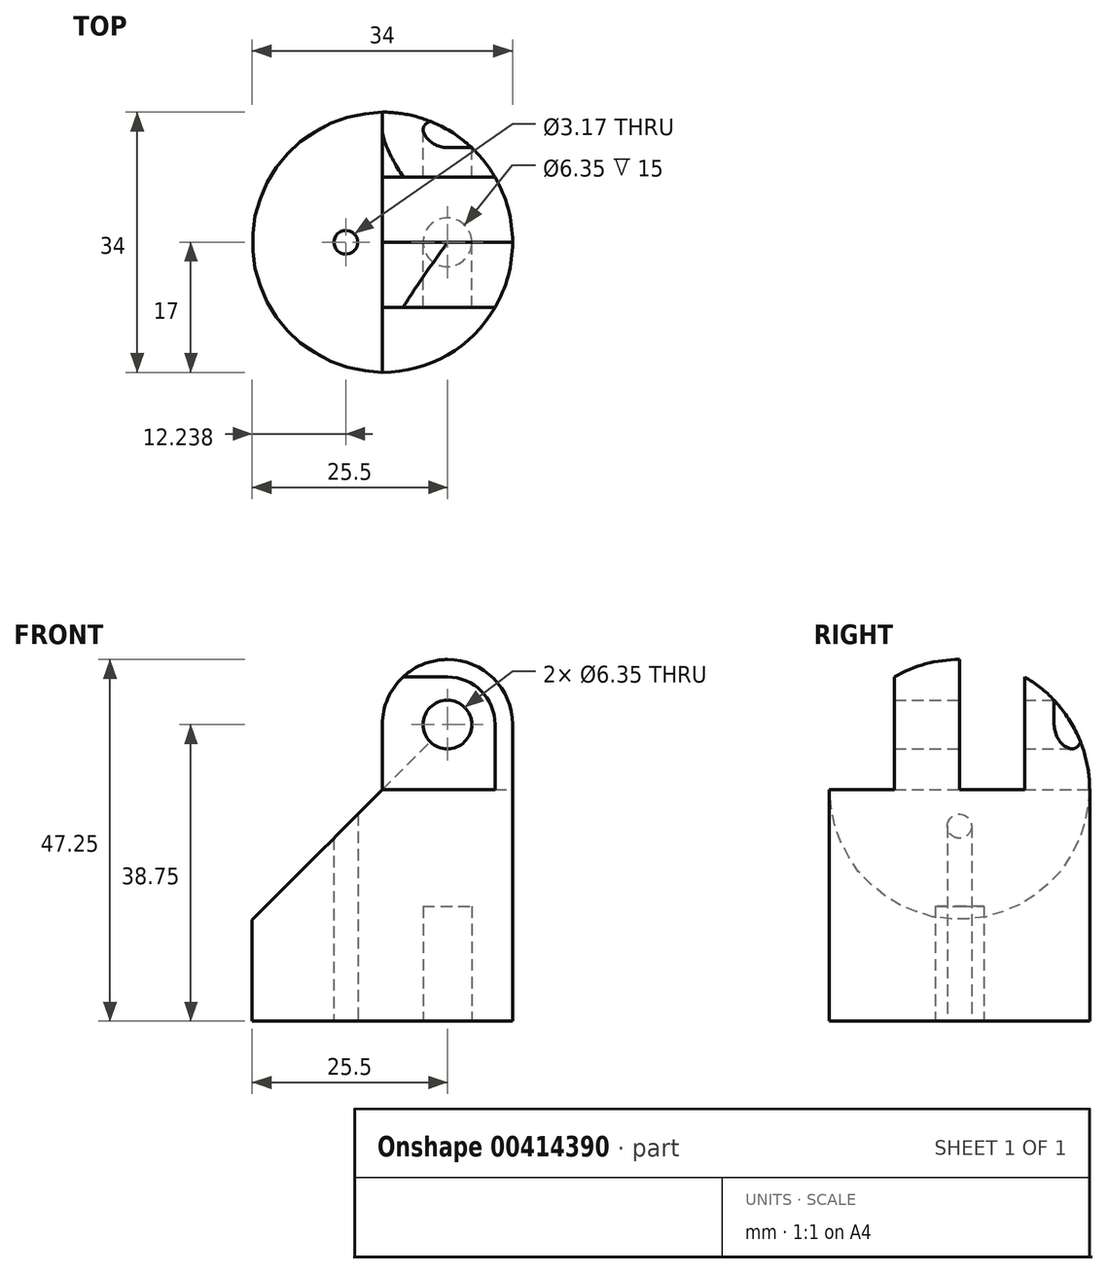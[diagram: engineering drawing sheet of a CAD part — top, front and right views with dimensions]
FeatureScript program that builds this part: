
annotation { "Feature Type Name" : "Feature", "Feature Type Description" : "" }
export const myFeature = defineFeature(function(context is Context, id is Id, definition is map)
    precondition{}
    {
        {
            var Q0;
            Q0=qCreatedBy(makeId("Top.planeOp"),FACE);
            var sketch = newSketch(context, id + "F0", { "sketchPlane" : qUnion([Q0])});
            skCircle(sketch, "E0", {"center": v(0, 0) * mm, "radius": 17 * mm});
            skSolve(sketch);
        }
        {
            var Q0;
            Q0 = qSketchRegion(id + "F0", true);
            extrude(context, id + "F1", {"entities" : qUnion([Q0]), "offsetDistance" : 25 * mm, "depth" : 13.25 * mm});
        }
        {
            var Q0;
            Q0=qCreatedBy(makeId("Front.planeOp"),FACE);
            var sketch = newSketch(context, id + "F2", { "sketchPlane" : qUnion([Q0])});
            skLineSegment(sketch, "E1", {"start": v(17, 38.75) * mm, "end": v(17, 13.25) * mm});
            skLineSegment(sketch, "E2", {"start": v(17, 13.25) * mm, "end": v(-17, 13.25) * mm});
            skLineSegment(sketch, "E3", {"start": v(-17, 13.25) * mm, "end": v(0, 30.25) * mm});
            skLineSegment(sketch, "E4", {"start": v(0, 30.25) * mm, "end": v(0, 38.75) * mm});
            skArc(sketch, "E5", {"start": v(0, 38.75) * mm, "mid": v(8.5, 47.25) * mm, "end": v(17, 38.75) * mm});
            skPoint(sketch, "E6", {"position": v(0, 13.25) * mm});
            skCircle(sketch, "E7", {"center": v(8.5, 38.75) * mm, "radius": 3.18 * mm});
            skSolve(sketch);
        }
        {
            var Q0;
            Q0 = qSketchRegion(id + "F2", true);
            var Q1;
            Q1=makeQuery(id+"F1.opExtrude","SWEPT_FACE",FACE,{"disambiguationData":[OSD([sQuery(id+"F0.wireOp",EDGE,"E0")])]});
            extrude(context, id + "F3", {"entities" : qUnion([Q0]), "operationType" : NewBodyOperationType.ADD, "endBound" : BoundingType.UP_TO_SURFACE, "endBoundEntityFace" : qUnion([Q1]), "depth" : 25 * mm});
        }
        {
            var Q0;
            Q0 = qSketchRegion(id + "F2", true);
            var Q1;
            {var subQ0=sQuery(id+"F0.wireOp",EDGE,"E0");Q1=makeQuery(id+"F3.boolean.opBoolean","MERGE",FACE,{"derivedFrom":[makeQuery(id+"F1.opExtrude","SWEPT_FACE",FACE,{"disambiguationData":[OSD([subQ0])]}),makeQuery(id+"F3.opExtrude","CAP_FACE",FACE,{"disambiguationData":[OSD([subQ0])],"isStart":false})]});}
            extrude(context, id + "F4", {"entities" : qUnion([Q0]), "operationType" : NewBodyOperationType.ADD, "endBound" : BoundingType.UP_TO_SURFACE, "oppositeDirection" : true, "endBoundEntityFace" : qUnion([Q1]), "depth" : 25 * mm});
        }
        {
            var Q0;
            Q0=qCreatedBy(makeId("Top.planeOp"),FACE);
            cPlane(context, id + "F5", {"entities" : qUnion([Q0]), "cplaneType" : CPlaneType.OFFSET, "offset" : 54 * mm, "width" : 150 * mm, "height" : 150 * mm});
        }
        {
            var Q0;
            Q0=qCreatedBy(id+"F5.planeOp",FACE);
            var sketch = newSketch(context, id + "F6", { "sketchPlane" : qUnion([Q0])});
            skLineSegment(sketch, "E8.bottom", {"start": v(0, 0) * mm, "end": v(17, 0) * mm});
            skLineSegment(sketch, "E8.top", {"start": v(0, 8.5) * mm, "end": v(17, 8.5) * mm});
            skLineSegment(sketch, "E8.left", {"start": v(0, 0) * mm, "end": v(0, 8.5) * mm});
            skLineSegment(sketch, "E8.right", {"start": v(17, 0) * mm, "end": v(17, 8.5) * mm});
            skLineSegment(sketch, "E9.bottom", {"start": v(0, -17) * mm, "end": v(17, -17) * mm});
            skLineSegment(sketch, "E9.top", {"start": v(0, -8.5) * mm, "end": v(17, -8.5) * mm});
            skLineSegment(sketch, "E9.left", {"start": v(0, -17) * mm, "end": v(0, -8.5) * mm});
            skLineSegment(sketch, "E9.right", {"start": v(17, -17) * mm, "end": v(17, -8.5) * mm});
            skLineSegment(sketch, "E10", {"start": v(0, 0) * mm, "end": v(0, 17) * mm});
            skSolve(sketch);
        }
        {
            var Q0;
            Q0 = qSketchRegion(id + "F6", true);
            var Q1;
            Q1=makeQuery(id+"F3.opExtrude","CAP_VERTEX",VERTEX,{"disambiguationData":[OSD([sQuery(id+"F0.wireOp",EDGE,"E0"),sQuery(id+"F2.wireOp",EDGE,"E3"),sQuery(id+"F2.wireOp",EDGE,"E4")])],"isStart":false});
            extrude(context, id + "F7", {"entities" : qUnion([Q0]), "operationType" : NewBodyOperationType.REMOVE, "endBound" : BoundingType.UP_TO_VERTEX, "oppositeDirection" : true, "endBoundEntityVertex" : qUnion([Q1]), "depth" : 10 * mm});
        }
        {
            var Q0;
            Q0=qCreatedBy(makeId("Top.planeOp"),FACE);
            var sketch = newSketch(context, id + "F8", { "sketchPlane" : qUnion([Q0])});
            skCircle(sketch, "E11", {"center": v(-4.76, 0) * mm, "radius": 1.59 * mm});
            skLineSegment(sketch, "E12", {"start": v(0, 0) * mm, "end": v(-17, 0) * mm});
            skSolve(sketch);
        }
        {
            var Q0;
            Q0 = qSketchRegion(id + "F8", true);
            extrude(context, id + "F9", {"entities" : qUnion([Q0]), "operationType" : NewBodyOperationType.REMOVE, "endBound" : BoundingType.THROUGH_ALL, "depth" : 25 * mm});
        }
        {
            var Q0;
            Q0=makeQuery(id+"F1.opExtrude","CAP_FACE",FACE,{"disambiguationData":[OSD([sQuery(id+"F0.wireOp",EDGE,"E0")])],"isStart":true});
            var sketch = newSketch(context, id + "F10", { "sketchPlane" : qUnion([Q0])});
            skCircle(sketch, "E13", {"center": v(8.5, 0) * mm, "radius": 3.18 * mm});
            skLineSegment(sketch, "E14", {"start": v(0, 0) * mm, "end": v(17, 0) * mm});
            skSolve(sketch);
        }
        {
            var Q0;
            Q0 = qSketchRegion(id + "F10", true);
            extrude(context, id + "F11", {"entities" : qUnion([Q0]), "operationType" : NewBodyOperationType.REMOVE, "oppositeDirection" : true, "depth" : 15 * mm});
        }
        {
            var Q0;
            Q0=qCreatedBy(makeId("Right.planeOp"),FACE);
            cPlane(context, id + "F12", {"entities" : qUnion([Q0]), "cplaneType" : CPlaneType.OFFSET, "offset" : 8.5 * mm, "width" : 150 * mm, "height" : 150 * mm});
        }
        {
            var Q0;
            Q0=qCreatedBy(id+"F12.planeOp",FACE);
            var sketch = newSketch(context, id + "F13", { "sketchPlane" : qUnion([Q0])});
            skLineSegment(sketch, "E15.bottom", {"start": v(17, 30.25) * mm, "end": v(-17, 30.25) * mm});
            skLineSegment(sketch, "E15.top", {"start": v(17, 47.25) * mm, "end": v(-17, 47.25) * mm});
            skLineSegment(sketch, "E15.left", {"start": v(17, 30.25) * mm, "end": v(17, 47.25) * mm});
            skLineSegment(sketch, "E15.right", {"start": v(-17, 30.25) * mm, "end": v(-17, 47.25) * mm});
            skArc(sketch, "E16", {"start": v(17, 30.25) * mm, "mid": v(0, 47.25) * mm, "end": v(-17, 30.25) * mm});
            skLineSegment(sketch, "E17", {"start": v(17, 38.75) * mm, "end": v(-17, 38.75) * mm});
            skSolve(sketch);
        }
        {
            var Q0;
            {var subQ0=sQuery(id+"F13.wireOp",EDGE,"E15.left");Q0=makeQuery(id+"F13.imprint","IMPRINT",FACE,{"disambiguationData":[TD([[makeQuery(id+"F13.imprint","IMPRINT",EDGE,{"derivedFrom":subQ0}),1.0]])]});}
            var Q1;
            {var subQ0=sQuery(id+"F13.wireOp",EDGE,"E15.right");Q1=makeQuery(id+"F13.imprint","IMPRINT",FACE,{"disambiguationData":[TD([[makeQuery(id+"F13.imprint","IMPRINT",EDGE,{"derivedFrom":subQ0}),-1.0]])]});}
            var Q2;
            {var subQ0=sQuery(id+"F13.wireOp",EDGE,"E15.right");var subQ1=sQuery(id+"F13.wireOp",EDGE,"E15.top");var subQ2=makeQuery(id+"F13.imprint","INTERSECT",VERTEX,{"derivedFrom":[subQ1,subQ0]});Q2=makeQuery(id+"F13.imprint","IMPRINT",FACE,{"disambiguationData":[TD([[makeQuery(id+"F13.imprint","IMPRINT",EDGE,{"disambiguationData":[TD([[subQ2,1.0]])],"derivedFrom":subQ1}),1.0]])]});}
            var Q3;
            {var subQ0=sQuery(id+"F13.wireOp",EDGE,"E15.left");var subQ1=sQuery(id+"F13.wireOp",EDGE,"E15.top");var subQ2=makeQuery(id+"F13.imprint","INTERSECT",VERTEX,{"derivedFrom":[subQ1,subQ0]});Q3=makeQuery(id+"F13.imprint","IMPRINT",FACE,{"disambiguationData":[TD([[makeQuery(id+"F13.imprint","IMPRINT",EDGE,{"disambiguationData":[TD([[subQ2,-1.0]])],"derivedFrom":subQ1}),1.0]])]});}
            extrude(context, id + "F14", {"entities" : qUnion([Q0, Q1, Q2, Q3]), "operationType" : NewBodyOperationType.REMOVE, "oppositeDirection" : true, "depth" : 34 * mm});
        }
        {
            var Q0;
            {var subQ0=sQuery(id+"F13.wireOp",EDGE,"E15.left");var subQ1=sQuery(id+"F13.wireOp",EDGE,"E15.top");var subQ2=makeQuery(id+"F13.imprint","INTERSECT",VERTEX,{"derivedFrom":[subQ1,subQ0]});Q0=makeQuery(id+"F13.imprint","IMPRINT",FACE,{"disambiguationData":[TD([[makeQuery(id+"F13.imprint","IMPRINT",EDGE,{"disambiguationData":[TD([[subQ2,-1.0]])],"derivedFrom":subQ1}),1.0]])]});}
            var Q1;
            {var subQ0=sQuery(id+"F13.wireOp",EDGE,"E15.right");var subQ1=sQuery(id+"F13.wireOp",EDGE,"E15.top");var subQ2=makeQuery(id+"F13.imprint","INTERSECT",VERTEX,{"derivedFrom":[subQ1,subQ0]});Q1=makeQuery(id+"F13.imprint","IMPRINT",FACE,{"disambiguationData":[TD([[makeQuery(id+"F13.imprint","IMPRINT",EDGE,{"disambiguationData":[TD([[subQ2,1.0]])],"derivedFrom":subQ1}),1.0]])]});}
            var Q2;
            Q2=sQuery(id+"F13.wireOp",EDGE,"E17");
            revolve(context, id + "F15", {"operationType" : NewBodyOperationType.REMOVE, "entities" : qUnion([Q0, Q1]), "axis" : qUnion([Q2]), "revolveType" : RevolveType.ONE_DIRECTION, "oppositeDirection" : true, "angle" : 90 * degree});
        }
    });
